# Revit family: HUNTER_RAIN-CLIK
name_source: partatom
category: Electrical Fixtures
revit_build: Autodesk Revit 2017 (Build: 20190508_0315(x64)
units: mm (PartAtom-declared; Revit-internal decimal feet)

## family parameters
Cut with Voids When Loaded = No
Host = Face
Maintain Annotation Orientation = No
OmniClass Number = 23.27.11.11.23
Part Type = Normal
Room Calculation Point = No
Round Connector Dimension = Use Diameter
Shared = Yes

## types (2) — shared parameters
16_AWG = No
18_AWG = No
20_AWG = Yes
Assembly Code = G4030100
Current = 3 A
Default Elevation = 1219 mm
Distance Coverage = 60000 mm  [stored 196.85 ft]
Frequency = 433000000 Hz
Input Voltage = 24 V
Keynote = 32 84 23.05
Manufacturer = Hunter® Industries
Power = 72 VA
Sensor Coverage Zone = Yes
Sensor Height = 60 mm  [stored 0.19685 ft]
Sensor Length = 180 mm  [stored 0.590551 ft]
Sensor Symbol = Yes
Sensor Wiring = Wired 7.6m of 0.5mm² sheathed, two-conductor, UL-approved wire
URL = https://www.hunterindustries.com
WireType_Range_15_30_Meter = 15000 mm  [stored 49.2126 ft]

## per-type parameters (varying)
| type | Description | Freeze Sensor | RAIN-CLIK® Model | Type Comments |
| RAIN-CLIK | RAIN-CLIK® Wired Rain Sensor with built in Quick Response ™ Technology | No | Wired Rain-Clik sensor | RAIN-CLIK® Sensor |
| RFC | RFC® Wired Rain and Freeze Sensor with built in Quick Response ™ Technology | Yes | Wired Rain and Freeze-Clik sensor | RFC ® Sensor |

note: column(s) folded — value = type name in every type: Model

note: [stored X ft] marks values corroborated as IEEE doubles in the binary element streams (Revit-internal decimal feet)

## geometry (parser evidence)
native form markers: Sweep x8
no freeform markers — native parametric forms only
